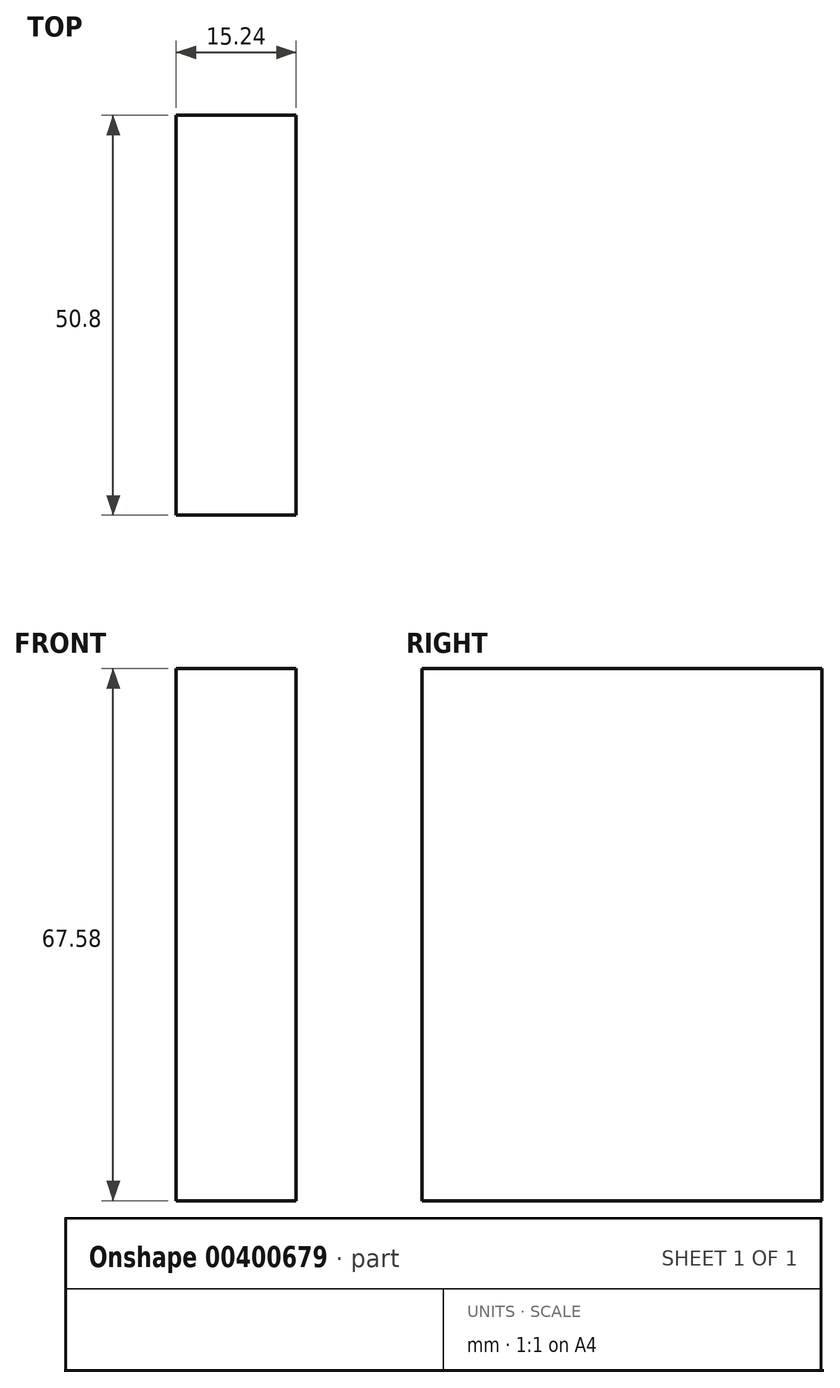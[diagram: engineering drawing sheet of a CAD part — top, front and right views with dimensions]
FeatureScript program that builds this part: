
annotation { "Feature Type Name" : "Feature", "Feature Type Description" : "" }
export const myFeature = defineFeature(function(context is Context, id is Id, definition is map)
    precondition{}
    {
        {
            var Q0;
            Q0=qCreatedBy(makeId("Front.planeOp"),FACE);
            var sketch = newSketch(context, id + "F0", { "sketchPlane" : qUnion([Q0])});
            skLineSegment(sketch, "E0.bottom", {"start": v(0, 22.08) * mm, "end": v(15.24, 22.08) * mm});
            skLineSegment(sketch, "E0.top", {"start": v(0, 89.66) * mm, "end": v(15.24, 89.66) * mm});
            skLineSegment(sketch, "E0.left", {"start": v(0, 22.08) * mm, "end": v(0, 89.66) * mm});
            skLineSegment(sketch, "E0.right", {"start": v(15.24, 22.08) * mm, "end": v(15.24, 89.66) * mm});
            skSolve(sketch);
        }
        {
            var Q0;
            Q0 = qSketchRegion(id + "FhEtRkYwVQNWWxn_0", true);
            var Q1;
            Q1=makeQuery(id+"F0.imprint","IMPRINT",FACE,{"disambiguationData":[TD([[makeQuery(id+"F0.imprint","IMPRINT",EDGE,{"derivedFrom":sQuery(id+"F0.wireOp",EDGE,"E0.bottom")}),1.0]])]});
            extrude(context, id + "F1", {"entities" : qUnion([Q0, Q1]), "oppositeDirection" : true, "depth" : 50.8 * mm});
        }
    });
